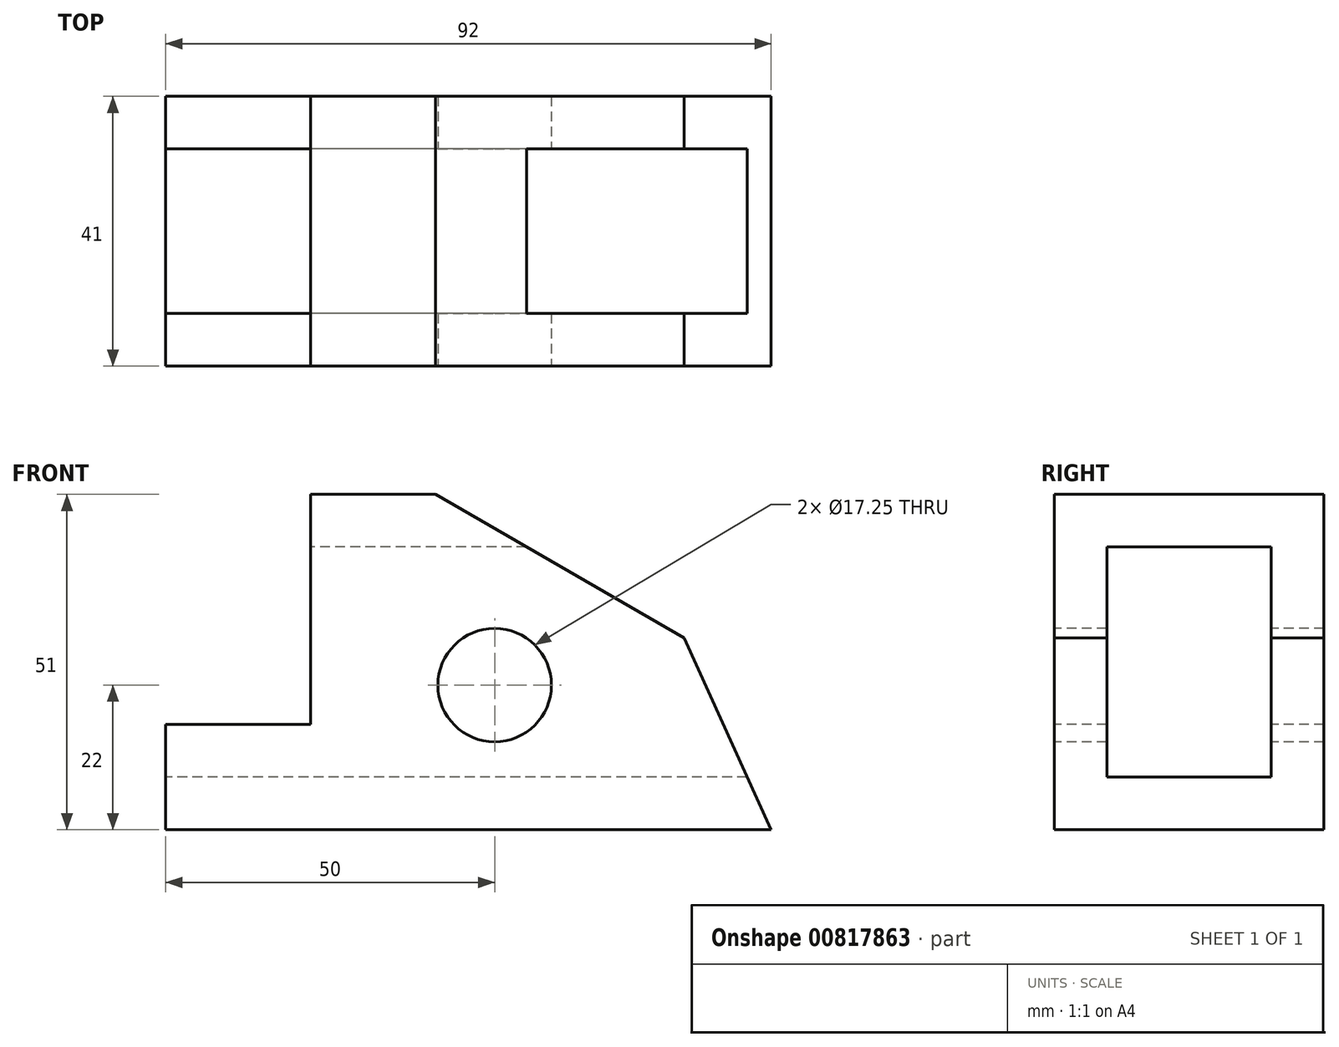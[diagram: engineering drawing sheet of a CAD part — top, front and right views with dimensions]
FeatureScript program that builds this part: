
annotation { "Feature Type Name" : "Feature", "Feature Type Description" : "" }
export const myFeature = defineFeature(function(context is Context, id is Id, definition is map)
    precondition{}
    {
        {
            var Q0;
            Q0=qCreatedBy(makeId("Front.planeOp"),FACE);
            var sketch = newSketch(context, id + "F0", { "sketchPlane" : qUnion([Q0])});
            skLineSegment(sketch, "E0", {"start": v(0, 0) * mm, "end": v(0, 16) * mm});
            skLineSegment(sketch, "E1", {"start": v(0, 16) * mm, "end": v(22, 16) * mm});
            skLineSegment(sketch, "E2", {"start": v(22, 16) * mm, "end": v(22, 51) * mm});
            skLineSegment(sketch, "E3", {"start": v(22, 51) * mm, "end": v(41, 51) * mm});
            skLineSegment(sketch, "E4", {"start": v(41, 51) * mm, "end": v(78.82, 29.16) * mm});
            skLineSegment(sketch, "E5", {"start": v(78.82, 29.16) * mm, "end": v(92, 0) * mm});
            skLineSegment(sketch, "E6", {"start": v(92, 0) * mm, "end": v(0, 0) * mm});
            skLineSegment(sketch, "E7", {"start": v(41, 51) * mm, "end": v(70.03, 51) * mm});
            skSolve(sketch);
        }
        {
            var Q0;
            Q0 = qSketchRegion(id + "F0", true);
            extrude(context, id + "F1", {"entities" : qUnion([Q0]), "oppositeDirection" : true, "depth" : 41 * mm, "offsetDistance" : 25 * mm});
        }
        {
            var Q0;
            Q0=qCreatedBy(makeId("Right.planeOp"),FACE);
            var sketch = newSketch(context, id + "F2", { "sketchPlane" : qUnion([Q0])});
            skLineSegment(sketch, "E8.bottom", {"start": v(8, 8) * mm, "end": v(33, 8) * mm});
            skLineSegment(sketch, "E8.top", {"start": v(8, 43) * mm, "end": v(33, 43) * mm});
            skLineSegment(sketch, "E8.left", {"start": v(8, 8) * mm, "end": v(8, 43) * mm});
            skLineSegment(sketch, "E8.right", {"start": v(33, 8) * mm, "end": v(33, 43) * mm});
            skSolve(sketch);
        }
        {
            var Q0;
            Q0 = qSketchRegion(id + "F2", true);
            extrude(context, id + "F3", {"entities" : qUnion([Q0]), "operationType" : NewBodyOperationType.REMOVE, "endBound" : BoundingType.THROUGH_ALL, "depth" : 25 * mm, "offsetDistance" : 25 * mm});
        }
        {
            var Q0;
            Q0=makeQuery(id+"F1.opExtrude","CAP_FACE",FACE,{"disambiguationData":[OSD([sQuery(id+"F0.wireOp",EDGE,"E0"),sQuery(id+"F0.wireOp",EDGE,"E1"),sQuery(id+"F0.wireOp",EDGE,"E2"),sQuery(id+"F0.wireOp",EDGE,"E3"),sQuery(id+"F0.wireOp",EDGE,"E4"),sQuery(id+"F0.wireOp",EDGE,"E5"),sQuery(id+"F0.wireOp",EDGE,"E6")])],"isStart":true});
            var sketch = newSketch(context, id + "F4", { "sketchPlane" : qUnion([Q0])});
            skCircle(sketch, "E9", {"center": v(50, 22) * mm, "radius": 8.62 * mm});
            skSolve(sketch);
        }
        {
            var Q0;
            Q0 = qSketchRegion(id + "F4", true);
            extrude(context, id + "F5", {"entities" : qUnion([Q0]), "operationType" : NewBodyOperationType.REMOVE, "endBound" : BoundingType.THROUGH_ALL, "oppositeDirection" : true, "depth" : 25 * mm, "offsetDistance" : 25 * mm});
        }
    });
